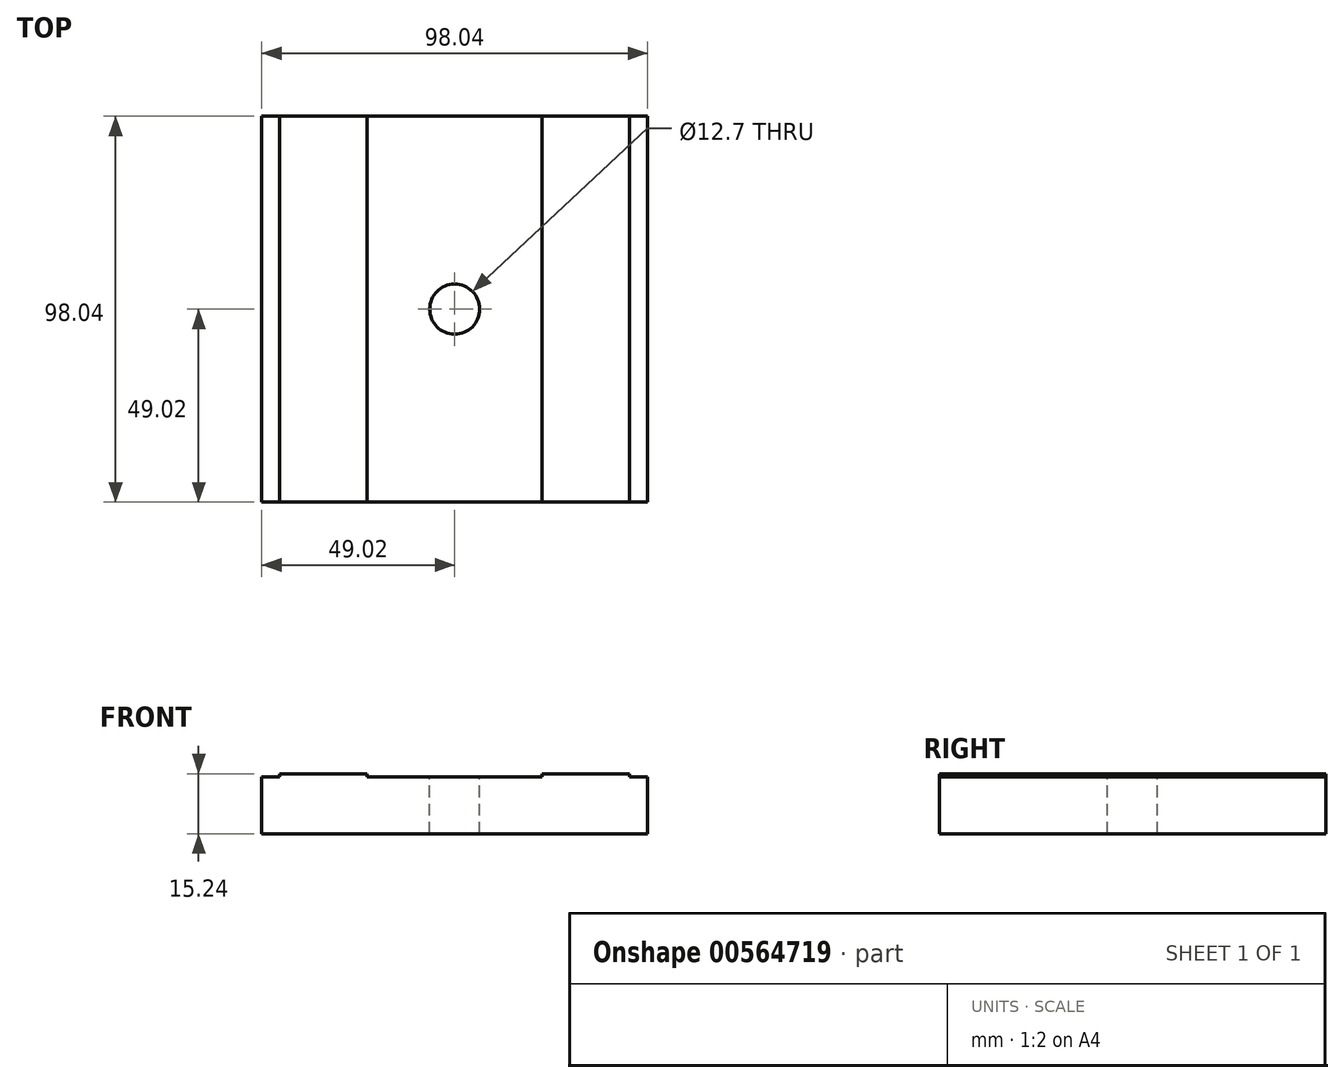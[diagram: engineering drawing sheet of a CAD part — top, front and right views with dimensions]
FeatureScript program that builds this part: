
annotation { "Feature Type Name" : "Feature", "Feature Type Description" : "" }
export const myFeature = defineFeature(function(context is Context, id is Id, definition is map)
    precondition{}
    {
        {
            var Q0;
            Q0=qCreatedBy(makeId("Top.planeOp"),FACE);
            var sketch = newSketch(context, id + "F0", { "sketchPlane" : qUnion([Q0])});
            skPoint(sketch, "E0.middle", {"position": v(0, 0) * mm});
            skLineSegment(sketch, "E1.bottom", {"start": v(-49.02, -49.02) * mm, "end": v(49.02, -49.02) * mm});
            skLineSegment(sketch, "E1.top", {"start": v(-49.02, 49.02) * mm, "end": v(49.02, 49.02) * mm});
            skLineSegment(sketch, "E1.left", {"start": v(-49.02, -49.02) * mm, "end": v(-49.02, 49.02) * mm});
            skLineSegment(sketch, "E1.right", {"start": v(49.02, -49.02) * mm, "end": v(49.02, 49.02) * mm});
            skSolve(sketch);
        }
        {
            var Q0;
            Q0=makeQuery(id+"F0.imprint","IMPRINT",FACE,{"disambiguationData":[TD([[makeQuery(id+"F0.imprint","IMPRINT",EDGE,{"derivedFrom":sQuery(id+"F0.wireOp",EDGE,"E1.bottom")}),1.0]])]});
            extrude(context, id + "F1", {"entities" : qUnion([Q0]), "depth" : 15.24 * mm, "offsetDistance" : 25.4 * mm});
        }
        {
            var Q0;
            Q0=makeQuery(id+"F1.opExtrude","CAP_FACE",FACE,{"disambiguationData":[OSD([sQuery(id+"F0.wireOp",EDGE,"E1.bottom"),sQuery(id+"F0.wireOp",EDGE,"E1.top"),sQuery(id+"F0.wireOp",EDGE,"E1.left"),sQuery(id+"F0.wireOp",EDGE,"E1.right")])],"isStart":false});
            var sketch = newSketch(context, id + "F2", { "sketchPlane" : qUnion([Q0])});
            skLineSegment(sketch, "E2", {"start": v(0, 49.02) * mm, "end": v(0, -49.02) * mm, "construction": true});
            skLineSegment(sketch, "E3", {"start": v(-25.4, 49.02) * mm, "end": v(-25.4, -49.02) * mm});
            skLineSegment(sketch, "E4", {"start": v(25.4, 49.02) * mm, "end": v(25.4, -49.02) * mm});
            skLineSegment(sketch, "E5", {"start": v(-22.23, 49.02) * mm, "end": v(-22.22, -49.02) * mm});
            skLineSegment(sketch, "E6", {"start": v(22.22, 49.02) * mm, "end": v(22.23, -49.02) * mm});
            skLineSegment(sketch, "E7", {"start": v(-44.45, 49.02) * mm, "end": v(-44.45, -49.02) * mm});
            skLineSegment(sketch, "E8", {"start": v(44.45, 49.02) * mm, "end": v(44.45, -49.02) * mm});
            skPoint(sketch, "E9", {"position": v(0, 0) * mm});
            skSolve(sketch);
        }
        {
            var Q0;
            Q0=sQuery(id+"F2.wireOp",VERTEX,"E9");
            var Q1;
            Q1=makeQuery(id+"F1.opExtrude","SWEPT_BODY",BODY,{"disambiguationData":[OSD([sQuery(id+"F0.wireOp",EDGE,"E1.bottom"),sQuery(id+"F0.wireOp",EDGE,"E1.top"),sQuery(id+"F0.wireOp",EDGE,"E1.left"),sQuery(id+"F0.wireOp",EDGE,"E1.right")])]});
            hole(context, id + "F3", {"style" : HoleStyle.SIMPLE, "endStyle" : HoleEndStyle.THROUGH, "holeDiameter" : 12.7 * mm, "isTappedThrough" : true, "tappedDepth" : 12.7 * mm, "tapClearance" : 3, "locations" : qUnion([Q0]), "scope" : qUnion([Q1])});
        }
        {
            var Q0;
            {var subQ0=sQuery(id+"F2.wireOp",EDGE,"E7");Q0=makeQuery(id+"F2.imprint","IMPRINT",FACE,{"disambiguationData":[TD([[makeQuery(id+"F2.imprint","IMPRINT",EDGE,{"derivedFrom":subQ0}),-1.0]])]});}
            var Q1;
            {var subQ0=sQuery(id+"F2.wireOp",EDGE,"E8");Q1=makeQuery(id+"F2.imprint","IMPRINT",FACE,{"disambiguationData":[TD([[makeQuery(id+"F2.imprint","IMPRINT",EDGE,{"derivedFrom":subQ0}),1.0]])]});}
            var Q2;
            {var subQ0=sQuery(id+"F2.wireOp",EDGE,"E5");Q2=makeQuery(id+"F2.imprint","IMPRINT",FACE,{"disambiguationData":[TD([[makeQuery(id+"F2.imprint","IMPRINT",EDGE,{"derivedFrom":subQ0}),1.0]])]});}
            extrude(context, id + "F4", {"entities" : qUnion([Q0, Q1, Q2]), "operationType" : NewBodyOperationType.REMOVE, "oppositeDirection" : true, "depth" : 0.79 * mm, "offsetDistance" : 25.4 * mm});
        }
    });
